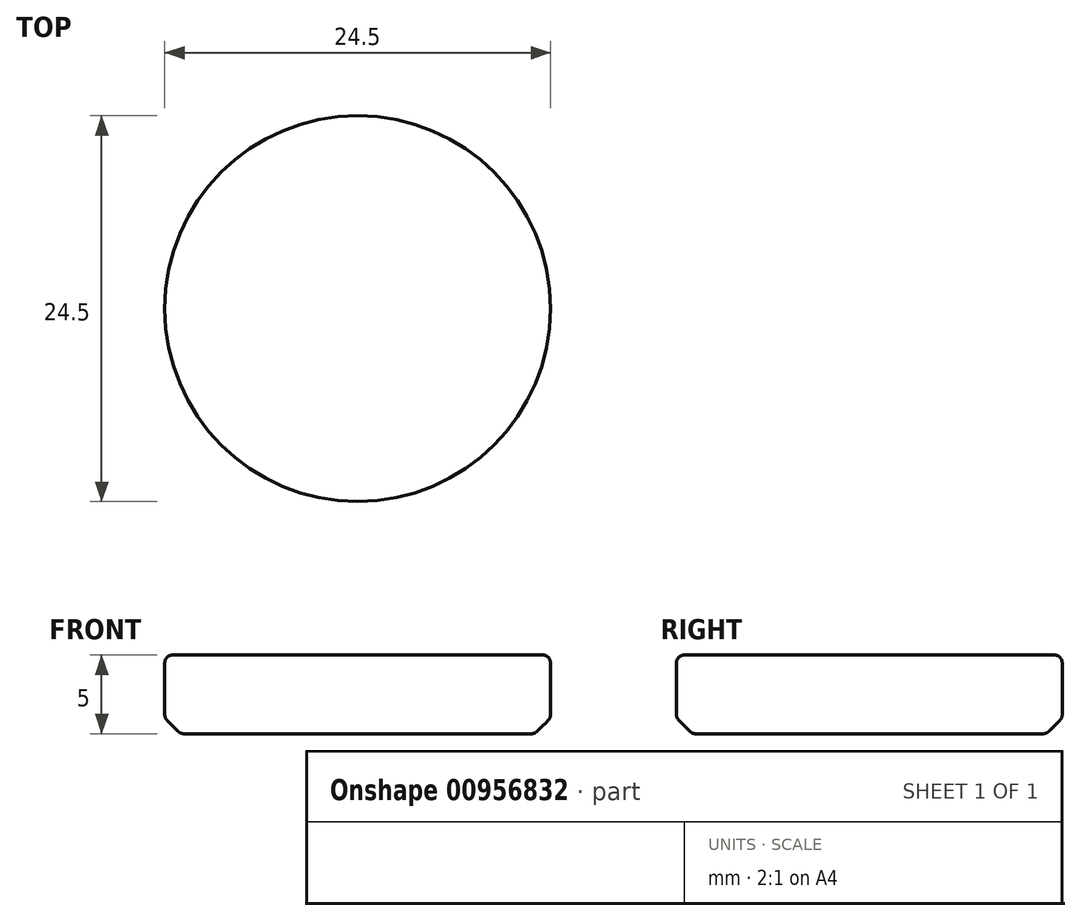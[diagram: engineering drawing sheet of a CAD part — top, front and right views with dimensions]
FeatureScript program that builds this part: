
annotation { "Feature Type Name" : "Feature", "Feature Type Description" : "" }
export const myFeature = defineFeature(function(context is Context, id is Id, definition is map)
    precondition{}
    {
        {
            var Q0;
            Q0=qCreatedBy(makeId("Top.planeOp"),FACE);
            var sketch = newSketch(context, id + "F0", { "sketchPlane" : qUnion([Q0])});
            skCircle(sketch, "E0", {"center": v(0, 0) * mm, "radius": 12.25 * mm});
            skSolve(sketch);
        }
        {
            var Q0;
            Q0=qSketchRegion(id+"F0",true);
            extrude(context, id + "F1", {"entities" : qUnion([Q0]), "depth" : 5 * mm, "offsetDistance" : 25.4 * mm});
        }
        {
            var Q0;
            Q0=makeQuery(id+"F1.opExtrude","CAP_EDGE",EDGE,{"disambiguationData":[OSD([sQuery(id+"F0.wireOp",EDGE,"E0")])],"isStart":true});
            chamfer(context, id + "F2", {"entities" : qUnion([Q0]), "width" : 1 * mm, "tangentPropagation" : true});
        }
        {
            var Q0;
            Q0=makeQuery(id+"F1.opExtrude","CAP_EDGE",EDGE,{"disambiguationData":[OSD([sQuery(id+"F0.wireOp",EDGE,"E0")])],"isStart":false});
            var Q1;
            {var subQ0=sQuery(id+"F0.wireOp",EDGE,"E0");Q1=makeQuery(id+"F2.opChamfer","BLEND_EDGE",EDGE,{"blendedFrom":[makeQuery(id+"F1.opExtrude","CAP_EDGE",EDGE,{"disambiguationData":[OSD([subQ0])],"isStart":true}),makeQuery(id+"F1.opExtrude","SWEPT_FACE",FACE,{"disambiguationData":[OSD([subQ0])]})],"blendedInto":[makeQuery(id+"F1.opExtrude","SWEPT_FACE",FACE,{"disambiguationData":[OSD([subQ0])]})]});}
            var Q2;
            {var subQ0=sQuery(id+"F0.wireOp",EDGE,"E0");Q2=makeQuery(id+"F2.opChamfer","BLEND_EDGE",EDGE,{"blendedFrom":[makeQuery(id+"F1.opExtrude","CAP_EDGE",EDGE,{"disambiguationData":[OSD([subQ0])],"isStart":true}),makeQuery(id+"F1.opExtrude","CAP_FACE",FACE,{"disambiguationData":[OSD([subQ0])],"isStart":true})],"blendedInto":[makeQuery(id+"F1.opExtrude","CAP_FACE",FACE,{"disambiguationData":[OSD([subQ0])],"isStart":true})]});}
            fillet(context, id + "F3", {"entities" : qUnion([Q0, Q1, Q2]), "radius" : .5 * mm, "tangentPropagation" : true, "allowEdgeOverflow" : false});
        }
    });
